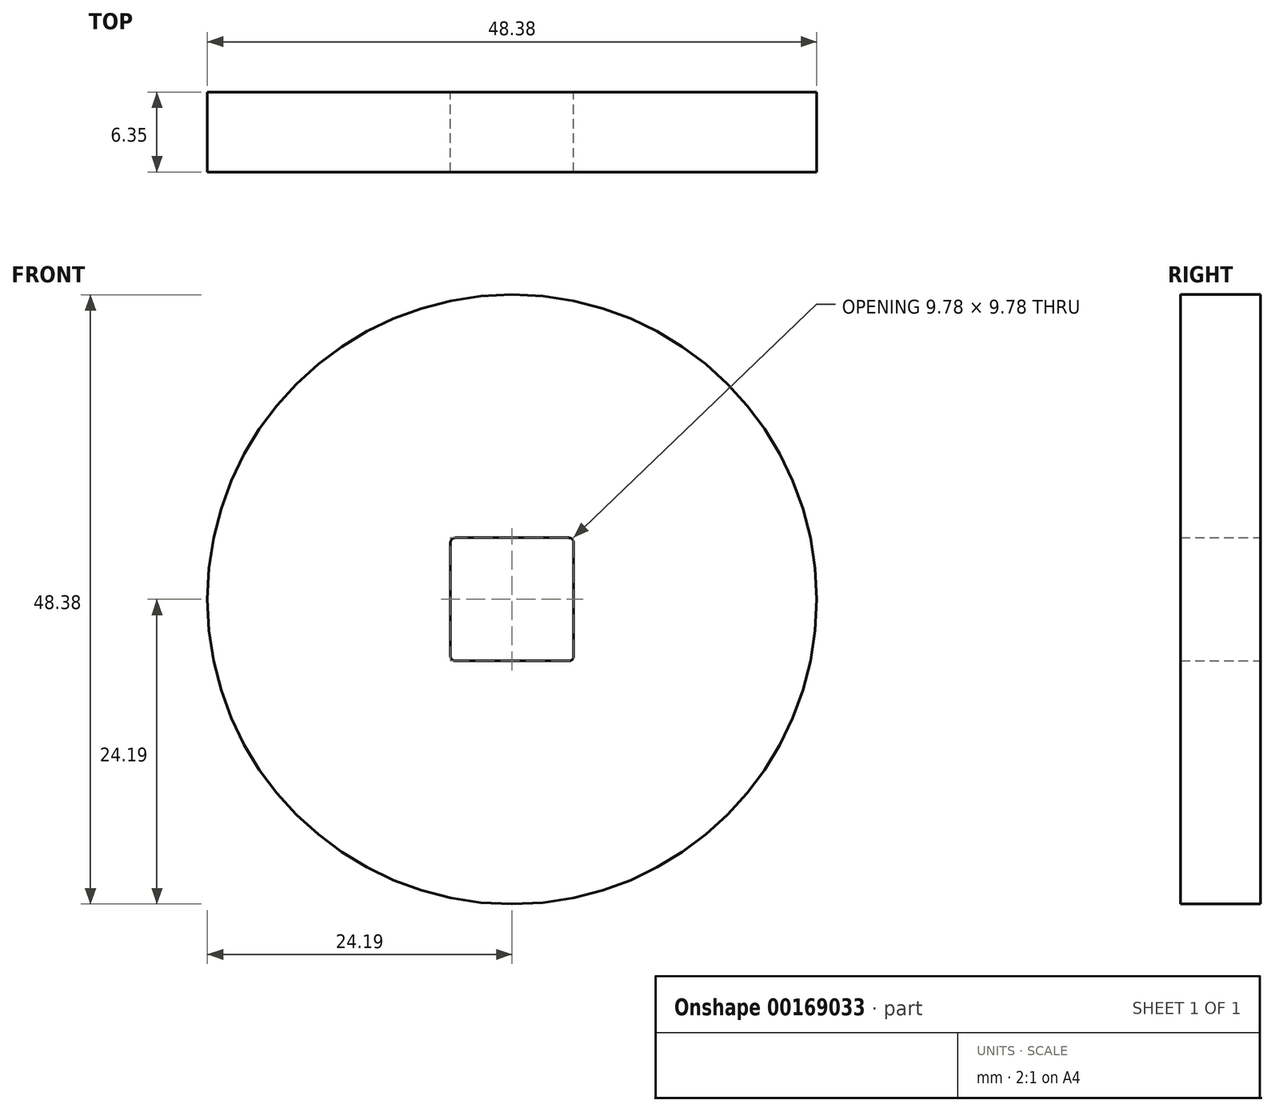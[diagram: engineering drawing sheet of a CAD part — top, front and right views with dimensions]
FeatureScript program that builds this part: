
annotation { "Feature Type Name" : "Feature", "Feature Type Description" : "" }
export const myFeature = defineFeature(function(context is Context, id is Id, definition is map)
    precondition{}
    {
        {
            var Q0;
            Q0=qCreatedBy(makeId("Front.planeOp"),FACE);
            var sketch = newSketch(context, id + "F0", { "sketchPlane" : qUnion([Q0])});
            skCircle(sketch, "E0", {"center": v(0, 0) * mm, "radius": 24.2 * mm});
            skLineSegment(sketch, "E1.bottom", {"start": v(-4.89, 4.89) * mm, "end": v(4.89, 4.89) * mm});
            skLineSegment(sketch, "E1.top", {"start": v(-4.89, -4.89) * mm, "end": v(4.89, -4.89) * mm});
            skLineSegment(sketch, "E1.left", {"start": v(-4.89, 4.89) * mm, "end": v(-4.89, -4.89) * mm});
            skLineSegment(sketch, "E1.right", {"start": v(4.89, 4.89) * mm, "end": v(4.89, -4.89) * mm});
            skSolve(sketch);
        }
        {
            var Q0;
            Q0=makeQuery(id+"F0.imprint","IMPRINT",FACE,{"disambiguationData":[TD([[makeQuery(id+"F0.imprint","IMPRINT",EDGE,{"derivedFrom":sQuery(id+"F0.wireOp",EDGE,"E0")}),1.0]])]});
            extrude(context, id + "F1", {"entities" : qUnion([Q0]), "depth" : 6.35 * mm});
        }
        {
            var Q0;
            Q0=makeQuery(id+"F1.opExtrude","SWEPT_EDGE",EDGE,{"disambiguationData":[OSD([sQuery(id+"F0.wireOp",EDGE,"E1.top"),sQuery(id+"F0.wireOp",EDGE,"E1.right")])]});
            var Q1;
            Q1=makeQuery(id+"F1.opExtrude","SWEPT_EDGE",EDGE,{"disambiguationData":[OSD([sQuery(id+"F0.wireOp",EDGE,"E1.bottom"),sQuery(id+"F0.wireOp",EDGE,"E1.right")])]});
            var Q2;
            Q2=makeQuery(id+"F1.opExtrude","SWEPT_EDGE",EDGE,{"disambiguationData":[OSD([sQuery(id+"F0.wireOp",EDGE,"E1.bottom"),sQuery(id+"F0.wireOp",EDGE,"E1.left")])]});
            var Q3;
            Q3=makeQuery(id+"F1.opExtrude","SWEPT_EDGE",EDGE,{"disambiguationData":[OSD([sQuery(id+"F0.wireOp",EDGE,"E1.top"),sQuery(id+"F0.wireOp",EDGE,"E1.left")])]});
            fillet(context, id + "F2", {"entities" : qUnion([Q0, Q1, Q2, Q3]), "radius" : 0.38 * mm, "tangentPropagation" : true, "allowEdgeOverflow" : false});
        }
    });
